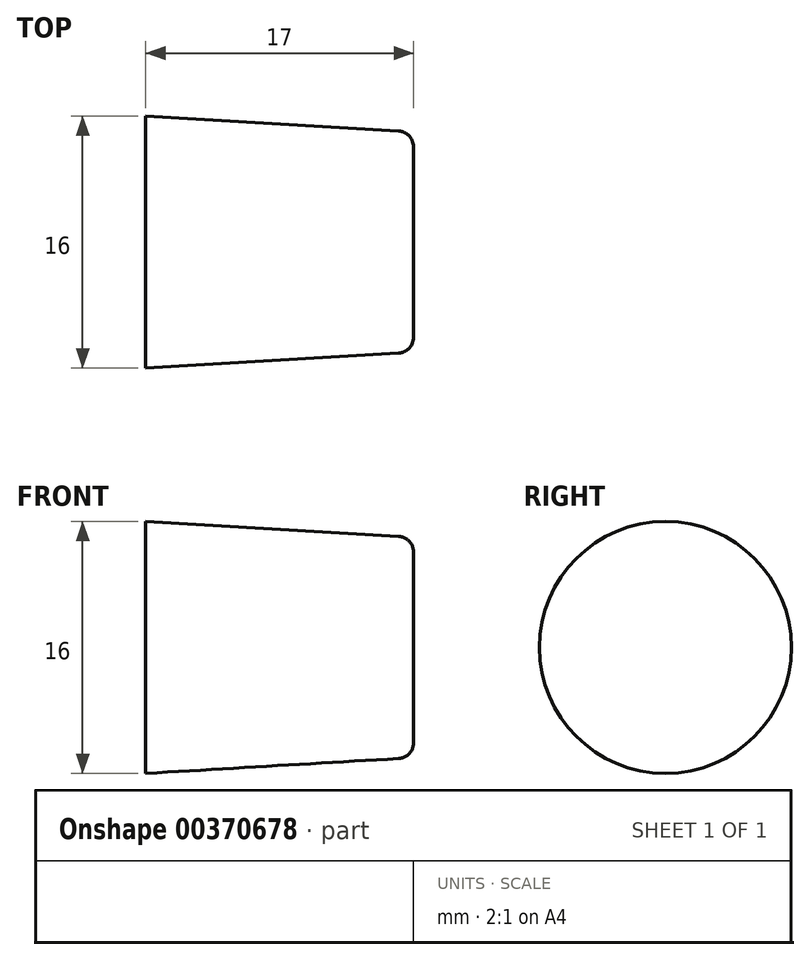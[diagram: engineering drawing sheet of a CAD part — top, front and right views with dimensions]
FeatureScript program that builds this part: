
annotation { "Feature Type Name" : "Feature", "Feature Type Description" : "" }
export const myFeature = defineFeature(function(context is Context, id is Id, definition is map)
    precondition{}
    {
        {
            var Q0;
            Q0=qCreatedBy(makeId("Front.planeOp"),FACE);
            var sketch = newSketch(context, id + "F0", { "sketchPlane" : qUnion([Q0])});
            skLineSegment(sketch, "E0", {"start": v(0, 0) * mm, "end": v(0, 8) * mm});
            skLineSegment(sketch, "E1", {"start": v(0, 8) * mm, "end": v(17, 7) * mm});
            skLineSegment(sketch, "E2", {"start": v(17, 7) * mm, "end": v(17, 0) * mm});
            skLineSegment(sketch, "E3", {"start": v(17, 0) * mm, "end": v(0, 0) * mm});
            skSolve(sketch);
        }
        {
            var Q0;
            Q0 = qSketchRegion(id + "F0", true);
            var Q1;
            Q1=sQuery(id+"F0.wireOp",EDGE,"E3");
            revolve(context, id + "F1", {"entities" : qUnion([Q0]), "axis" : qUnion([Q1]), "revolveType" : RevolveType.FULL});
        }
        {
            var Q0;
            Q0=makeQuery(id+"F1.opRevolve","SWEPT_EDGE",EDGE,{"disambiguationData":[OSD([sQuery(id+"F0.wireOp",EDGE,"E1"),sQuery(id+"F0.wireOp",EDGE,"E2")])]});
            fillet(context, id + "F2", {"entities" : qUnion([Q0]), "radius" : 1 * mm, "tangentPropagation" : true, "allowEdgeOverflow" : false});
        }
    });
